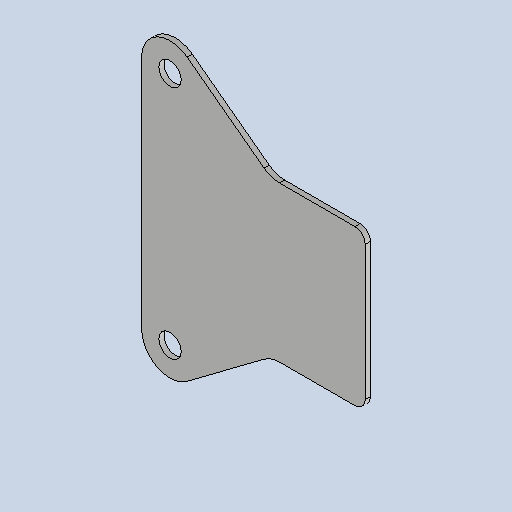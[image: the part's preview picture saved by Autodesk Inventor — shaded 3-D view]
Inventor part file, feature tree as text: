
AUTODESK INVENTOR PART (.ipt)
format: ipt  version: 2025 (Build 290162010, 162A)  size: 131,072 bytes
history: native  units: mm
features: sheet_metal_op x1, chamfer x1, mirror x1, sketch x1, other x1
ambient origin geometry x8: Origin, YZ Plane, XZ Plane, XY Plane, X Axis, Y Axis, Z Axis, Center Point
bodies: Solid1 (feature_tree)
feature tree (5):
  sheet_metal_op  "Face1"
  chamfer  "Corner Round2"
  mirror  "Mirror1"
  sketch  "Sketch1"  dims[d2=80.0mm d3=80.0mm d6=3.0mm d25=6.0mm d29=5.0mm d30=13.0mm d31=10.0mm d32=40.0mm d33=6.429331mm d34=5.0mm d35=15.0mm]
  other  "Plate1"
